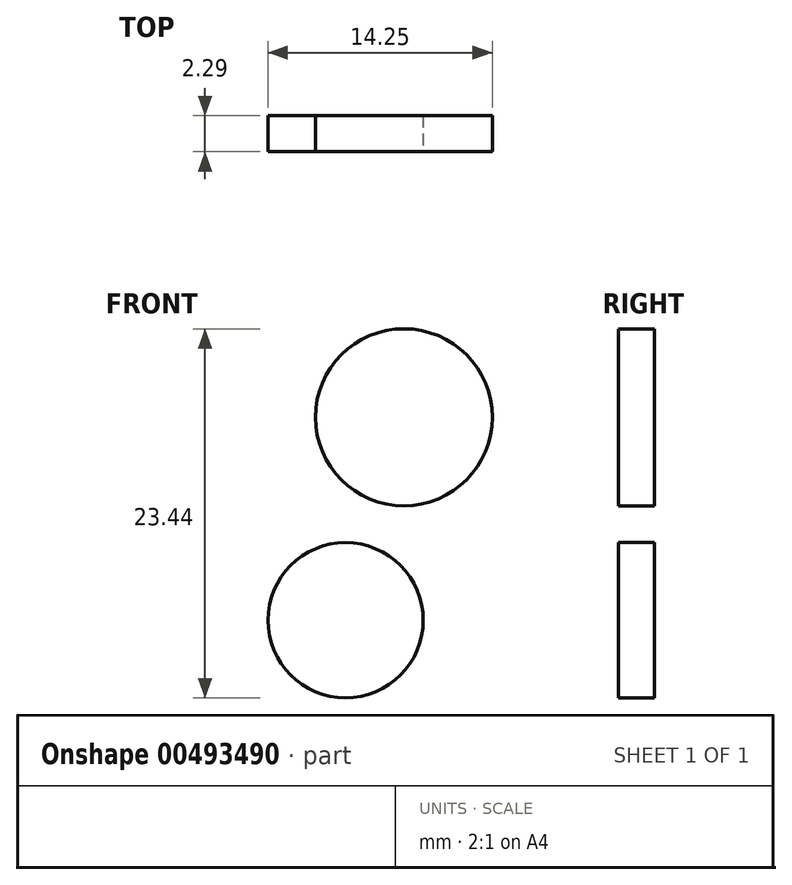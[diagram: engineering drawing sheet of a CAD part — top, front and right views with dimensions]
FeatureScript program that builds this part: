
annotation { "Feature Type Name" : "Feature", "Feature Type Description" : "" }
export const myFeature = defineFeature(function(context is Context, id is Id, definition is map)
    precondition{}
    {
        {
            var Q0;
            Q0=qCreatedBy(makeId("Front.planeOp"),FACE);
            var sketch = newSketch(context, id + "F0", { "sketchPlane" : qUnion([Q0])});
            skCircle(sketch, "E0", {"center": v(0, 0) * mm, "radius": 4.93 * mm});
            skCircle(sketch, "E1", {"center": v(3.7, 12.9) * mm, "radius": 5.62 * mm});
            skSolve(sketch);
        }
        {
            var Q0;
            Q0 = qSketchRegion(id + "F0", true);
            var Q1;
            Q1=sQuery(id+"F0.wireOp",EDGE,"E0");
            var Q2;
            Q2=sQuery(id+"F0.wireOp",EDGE,"E1");
            extrude(context, id + "F1", {"entities" : qUnion([Q0]), "bodyType" : ToolBodyType.SURFACE, "surfaceEntities" : qUnion([Q1, Q2]), "depth" : 2.3 * mm});
        }
    });
